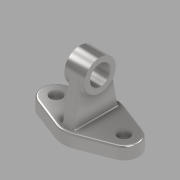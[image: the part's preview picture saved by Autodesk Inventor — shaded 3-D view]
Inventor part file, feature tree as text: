
AUTODESK INVENTOR PART (.ipt)
format: ipt  version: 2020 (Build 240168000, 168)  size: 227,328 bytes
history: native  units: mm
features: sketch x4, extrude x3, other x1, hole x1, fillet x1
ambient origin geometry x8: Origin, YZ Plane, XZ Plane, XY Plane, X Axis, Y Axis, Z Axis, Center Point
bodies: Body1 (feature_tree)
feature tree (10):
  other  "Sólido1"
  extrude  "PlacaBase"  Depth=44.0mm
  extrude  "Mástil"  Depth=18.0mm
  extrude  "CírculoSuperior"  Depth=18.0mm TaperAngle=0.0deg
  hole  "Agujero1"  [1 undecoded]
  fillet  "Empalme1"  Radius=46.0mm
  sketch  "Boceto1"  dims[d0=80.0mm d1=44.0mm]
  sketch  "Boceto2"  dims[d2=40.0mm d3=18.0mm]
  sketch  "Boceto3"  dims[d4=50.0mm d5=18.0mm d6=0.0mm]
  sketch  "Boceto4"  dims[d7=40.0mm d8=40.0mm d9=46.0mm d10=76.0mm d11=67.0mm d12=33.5mm d13=17.0mm d14=0.0mm d15=30.0mm d16=0.0mm d17=30.0mm d18=6.0mm d19=4.0mm d20=2.0mm d21=90.0deg d22=8.0mm d23=20.594885mm d24=3.0mm]
note: 1 required parameter value undecoded (feature->parameter linkage not recoverable at this tier; creation-order binding heuristic only, values carry confidence <= 0.55)
